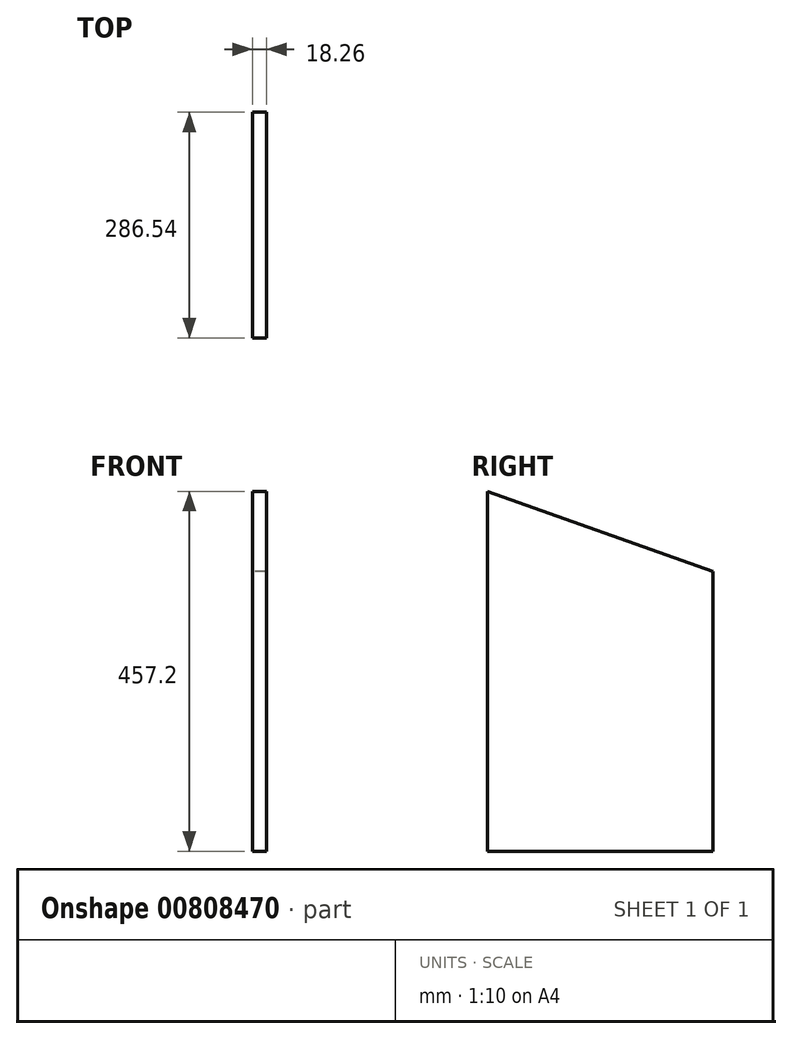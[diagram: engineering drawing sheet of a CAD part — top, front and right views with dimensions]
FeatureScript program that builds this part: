
annotation { "Feature Type Name" : "Feature", "Feature Type Description" : "" }
export const myFeature = defineFeature(function(context is Context, id is Id, definition is map)
    precondition{}
    {
        {
            var Q0;
            Q0=qCreatedBy(makeId("Right.planeOp"),FACE);
            var sketch = newSketch(context, id + "F0", { "sketchPlane" : qUnion([Q0])});
            skLineSegment(sketch, "E0", {"start": v(-180.7, -312.34) * mm, "end": v(-180.7, 144.86) * mm});
            skLineSegment(sketch, "E1", {"start": v(-180.7, 144.86) * mm, "end": v(105.85, 43.26) * mm});
            skLineSegment(sketch, "E2", {"start": v(105.85, 43.26) * mm, "end": v(105.85, -312.34) * mm});
            skLineSegment(sketch, "E3", {"start": v(105.85, -312.34) * mm, "end": v(-180.7, -312.34) * mm});
            skSolve(sketch);
        }
        {
            var Q0;
            Q0=makeQuery(id+"F0.imprint","IMPRINT",FACE,{"disambiguationData":[TD([[makeQuery(id+"F0.imprint","IMPRINT",EDGE,{"derivedFrom":sQuery(id+"F0.wireOp",EDGE,"E0")}),-1.0]])]});
            extrude(context, id + "F1", {"entities" : qUnion([Q0]), "depth" : 18.26 * mm, "offsetDistance" : 25.4 * mm});
        }
    });
